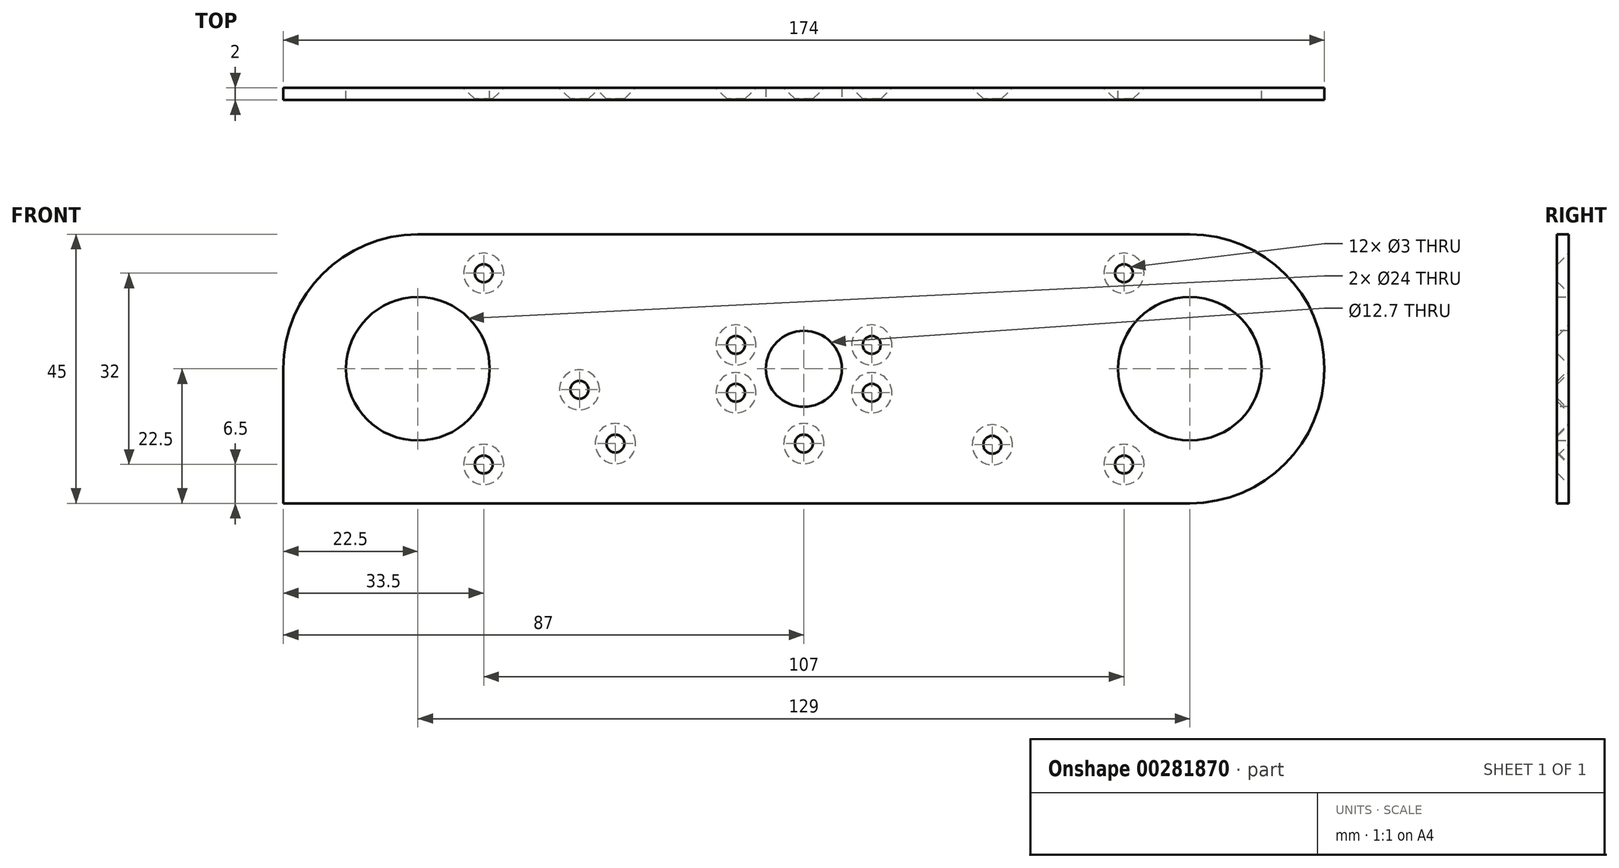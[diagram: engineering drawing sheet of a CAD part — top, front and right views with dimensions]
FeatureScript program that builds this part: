
annotation { "Feature Type Name" : "Feature", "Feature Type Description" : "" }
export const myFeature = defineFeature(function(context is Context, id is Id, definition is map)
    precondition{}
    {
        {
            var Q0;
            Q0=qCreatedBy(makeId("Front.planeOp"),FACE);
            var sketch = newSketch(context, id + "F0", { "sketchPlane" : qUnion([Q0])});
            skLineSegment(sketch, "E0.bottom", {"start": v(64.5, 22.5) * mm, "end": v(-64.5, 22.5) * mm});
            skLineSegment(sketch, "E0.top", {"start": v(64.5, -22.5) * mm, "end": v(-64.5, -22.5) * mm});
            skPoint(sketch, "E0.middle", {"position": v(0, 0) * mm});
            skCircle(sketch, "E1", {"center": v(64.5, 0) * mm, "radius": 12 * mm});
            skCircle(sketch, "E2", {"center": v(-64.5, 0) * mm, "radius": 12 * mm});
            skArc(sketch, "E3", {"start": v(-64.5, 22.5) * mm, "mid": v(-87, 0) * mm, "end": v(-64.5, -22.5) * mm});
            skArc(sketch, "E4", {"start": v(64.5, -22.5) * mm, "mid": v(87, 0) * mm, "end": v(64.5, 22.5) * mm});
            skPoint(sketch, "E5.orphan", {"position": v(-81.5, 22.5) * mm});
            skPoint(sketch, "E6.orphan", {"position": v(-81.5, -22.5) * mm});
            skPoint(sketch, "E7.orphan", {"position": v(81.5, 22.5) * mm});
            skPoint(sketch, "E8.orphan", {"position": v(81.5, -22.5) * mm});
            skSolve(sketch);
        }
        {
            var Q0;
            Q0=qSketchRegion(id+"F0",true);
            extrude(context, id + "F1", {"entities" : qUnion([Q0]), "depth" : 2 * mm});
        }
        {
            var Q0;
            Q0=makeQuery(id+"F1.opExtrude","CAP_FACE",FACE,{"disambiguationData":[OSD([sQuery(id+"F0.wireOp",EDGE,"E0.bottom"),sQuery(id+"F0.wireOp",EDGE,"E0.top"),sQuery(id+"F0.wireOp",EDGE,"E1"),sQuery(id+"F0.wireOp",EDGE,"E2"),sQuery(id+"F0.wireOp",EDGE,"E3"),sQuery(id+"F0.wireOp",EDGE,"E4")])],"isStart":false});
            var sketch = newSketch(context, id + "F2", { "sketchPlane" : qUnion([Q0])});
            skLineSegment(sketch, "E9.top", {"start": v(-64.5, -22.5) * mm, "end": v(-87, -22.5) * mm});
            skLineSegment(sketch, "E9.right", {"start": v(-87, 0) * mm, "end": v(-87, -22.5) * mm});
            skPoint(sketch, "E9.left.start.orphan", {"position": v(-64.5, 0) * mm});
            skLineSegment(sketch, "E10", {"start": v(-87, 0) * mm, "end": v(-80.88, 0) * mm});
            skLineSegment(sketch, "E11", {"start": v(-80.88, 0) * mm, "end": v(-78.27, -9.46) * mm});
            skLineSegment(sketch, "E12", {"start": v(-78.27, -9.46) * mm, "end": v(-70.55, -14.76) * mm});
            skLineSegment(sketch, "E13", {"start": v(-70.55, -14.76) * mm, "end": v(-64.5, -17.43) * mm});
            skLineSegment(sketch, "E14", {"start": v(-64.5, -17.43) * mm, "end": v(-64.5, -22.5) * mm});
            skSolve(sketch);
        }
        {
            var Q0;
            Q0=qSketchRegion(id+"F2",true);
            extrude(context, id + "F3", {"entities" : qUnion([Q0]), "operationType" : NewBodyOperationType.ADD, "oppositeDirection" : true, "depth" : 2 * mm});
        }
        {
            var Q0;
            Q0=makeQuery(id+"F3.boolean.opBoolean","MERGE",FACE,{"derivedFrom":[makeQuery(id+"F1.opExtrude","CAP_FACE",FACE,{"disambiguationData":[OSD([sQuery(id+"F0.wireOp",EDGE,"E0.bottom"),sQuery(id+"F0.wireOp",EDGE,"E0.top"),sQuery(id+"F0.wireOp",EDGE,"E1"),sQuery(id+"F0.wireOp",EDGE,"E2"),sQuery(id+"F0.wireOp",EDGE,"E3"),sQuery(id+"F0.wireOp",EDGE,"E4")])],"isStart":false}),makeQuery(id+"F3.opExtrude","CAP_FACE",FACE,{"disambiguationData":[OSD([sQuery(id+"F2.wireOp",EDGE,"E9.top"),sQuery(id+"F2.wireOp",EDGE,"E9.right"),sQuery(id+"F2.wireOp",EDGE,"E10"),sQuery(id+"F2.wireOp",EDGE,"E11"),sQuery(id+"F2.wireOp",EDGE,"E12"),sQuery(id+"F2.wireOp",EDGE,"E13"),sQuery(id+"F2.wireOp",EDGE,"E14")])],"isStart":true})]});
            var sketch = newSketch(context, id + "F4", { "sketchPlane" : qUnion([Q0])});
            skLineSegment(sketch, "E15.bottom", {"start": v(47, 22.5) * mm, "end": v(-47, 22.5) * mm, "construction": true});
            skLineSegment(sketch, "E15.top", {"start": v(47, -22.5) * mm, "end": v(-47, -22.5) * mm, "construction": true});
            skLineSegment(sketch, "E15.left", {"start": v(47, 22.5) * mm, "end": v(47, -22.5) * mm, "construction": true});
            skLineSegment(sketch, "E15.right", {"start": v(-47, 22.5) * mm, "end": v(-47, -22.5) * mm, "construction": true});
            skPoint(sketch, "E15.middle", {"position": v(0, 0) * mm});
            skLineSegment(sketch, "E16", {"start": v(-52.5, 0) * mm, "end": v(52.5, 0) * mm, "construction": true});
            skCircle(sketch, "E17", {"center": v(-53.5, 16) * mm, "radius": 1.5 * mm});
            skCircle(sketch, "E18", {"center": v(-53.5, -16) * mm, "radius": 1.5 * mm});
            skCircle(sketch, "E19", {"center": v(53.5, 16) * mm, "radius": 1.5 * mm});
            skCircle(sketch, "E20", {"center": v(53.5, -16) * mm, "radius": 1.5 * mm});
            skSolve(sketch);
        }
        {
            var Q0;
            Q0=qSketchRegion(id+"F4",true);
            extrude(context, id + "F5", {"entities" : qUnion([Q0]), "operationType" : NewBodyOperationType.REMOVE, "oppositeDirection" : true, "depth" : 25 * mm});
        }
        {
            var Q0;
            Q0=makeQuery(id+"F3.boolean.opBoolean","MERGE",FACE,{"derivedFrom":[makeQuery(id+"F1.opExtrude","CAP_FACE",FACE,{"disambiguationData":[OSD([sQuery(id+"F0.wireOp",EDGE,"E0.bottom"),sQuery(id+"F0.wireOp",EDGE,"E0.top"),sQuery(id+"F0.wireOp",EDGE,"E1"),sQuery(id+"F0.wireOp",EDGE,"E2"),sQuery(id+"F0.wireOp",EDGE,"E3"),sQuery(id+"F0.wireOp",EDGE,"E4")])],"isStart":false}),makeQuery(id+"F3.opExtrude","CAP_FACE",FACE,{"disambiguationData":[OSD([sQuery(id+"F2.wireOp",EDGE,"E9.top"),sQuery(id+"F2.wireOp",EDGE,"E9.right"),sQuery(id+"F2.wireOp",EDGE,"E10"),sQuery(id+"F2.wireOp",EDGE,"E11"),sQuery(id+"F2.wireOp",EDGE,"E12"),sQuery(id+"F2.wireOp",EDGE,"E13"),sQuery(id+"F2.wireOp",EDGE,"E14")])],"isStart":true})]});
            var sketch = newSketch(context, id + "F6", { "sketchPlane" : qUnion([Q0])});
            skCircle(sketch, "E21", {"center": v(0, 0) * mm, "radius": 6.35 * mm});
            skSolve(sketch);
        }
        {
            var Q0;
            Q0=qSketchRegion(id+"F6",true);
            extrude(context, id + "F7", {"entities" : qUnion([Q0]), "operationType" : NewBodyOperationType.REMOVE, "oppositeDirection" : true, "depth" : 25 * mm});
        }
        {
            var Q0;
            Q0=makeQuery(id+"F3.boolean.opBoolean","MERGE",FACE,{"derivedFrom":[makeQuery(id+"F1.opExtrude","CAP_FACE",FACE,{"disambiguationData":[OSD([sQuery(id+"F0.wireOp",EDGE,"E0.bottom"),sQuery(id+"F0.wireOp",EDGE,"E0.top"),sQuery(id+"F0.wireOp",EDGE,"E1"),sQuery(id+"F0.wireOp",EDGE,"E2"),sQuery(id+"F0.wireOp",EDGE,"E3"),sQuery(id+"F0.wireOp",EDGE,"E4")])],"isStart":false}),makeQuery(id+"F3.opExtrude","CAP_FACE",FACE,{"disambiguationData":[OSD([sQuery(id+"F2.wireOp",EDGE,"E9.top"),sQuery(id+"F2.wireOp",EDGE,"E9.right"),sQuery(id+"F2.wireOp",EDGE,"E10"),sQuery(id+"F2.wireOp",EDGE,"E11"),sQuery(id+"F2.wireOp",EDGE,"E12"),sQuery(id+"F2.wireOp",EDGE,"E13"),sQuery(id+"F2.wireOp",EDGE,"E14")])],"isStart":true})]});
            var sketch = newSketch(context, id + "F8", { "sketchPlane" : qUnion([Q0])});
            skPoint(sketch, "E22.middle", {"position": v(0, 0) * mm});
            skCircle(sketch, "E23", {"center": v(-11.35, 4) * mm, "radius": 1.5 * mm});
            skCircle(sketch, "E24", {"center": v(-11.35, -4) * mm, "radius": 1.5 * mm});
            skCircle(sketch, "E25", {"center": v(11.35, 4) * mm, "radius": 1.5 * mm});
            skCircle(sketch, "E26", {"center": v(11.35, -4) * mm, "radius": 1.5 * mm});
            skPoint(sketch, "E27.orphan", {"position": v(-11.35, 11.35) * mm});
            skPoint(sketch, "E28.orphan", {"position": v(11.35, 11.35) * mm});
            skPoint(sketch, "E22.top.start.orphan", {"position": v(11.35, -11.35) * mm});
            skPoint(sketch, "E29.orphan", {"position": v(-11.35, -11.35) * mm});
            skLineSegment(sketch, "E30", {"start": v(52.5, 0) * mm, "end": v(-52.5, 0) * mm, "construction": true});
            skLineSegment(sketch, "E31", {"start": v(-52.5, 0) * mm, "end": v(0, 0) * mm, "construction": true});
            skLineSegment(sketch, "E32", {"start": v(0, 22.5) * mm, "end": v(0, -22.5) * mm, "construction": true});
            skLineSegment(sketch, "E33.bottom", {"start": v(11.35, 11.35) * mm, "end": v(-11.35, 11.35) * mm, "construction": true});
            skLineSegment(sketch, "E33.top", {"start": v(11.35, -11.35) * mm, "end": v(-11.35, -11.35) * mm, "construction": true});
            skLineSegment(sketch, "E33.left", {"start": v(11.35, 11.35) * mm, "end": v(11.35, -11.35) * mm, "construction": true});
            skLineSegment(sketch, "E33.right", {"start": v(-11.35, 11.35) * mm, "end": v(-11.35, -11.35) * mm, "construction": true});
            skSolve(sketch);
        }
        {
            var Q0;
            Q0=qSketchRegion(id+"F8",true);
            extrude(context, id + "F9", {"entities" : qUnion([Q0]), "operationType" : NewBodyOperationType.REMOVE, "oppositeDirection" : true, "depth" : 25 * mm});
        }
        {
            var Q0;
            Q0=makeQuery(id+"F3.boolean.opBoolean","MERGE",FACE,{"derivedFrom":[makeQuery(id+"F1.opExtrude","CAP_FACE",FACE,{"disambiguationData":[OSD([sQuery(id+"F0.wireOp",EDGE,"E0.bottom"),sQuery(id+"F0.wireOp",EDGE,"E0.top"),sQuery(id+"F0.wireOp",EDGE,"E1"),sQuery(id+"F0.wireOp",EDGE,"E2"),sQuery(id+"F0.wireOp",EDGE,"E3"),sQuery(id+"F0.wireOp",EDGE,"E4")])],"isStart":false}),makeQuery(id+"F3.opExtrude","CAP_FACE",FACE,{"disambiguationData":[OSD([sQuery(id+"F2.wireOp",EDGE,"E9.top"),sQuery(id+"F2.wireOp",EDGE,"E9.right"),sQuery(id+"F2.wireOp",EDGE,"E10"),sQuery(id+"F2.wireOp",EDGE,"E11"),sQuery(id+"F2.wireOp",EDGE,"E12"),sQuery(id+"F2.wireOp",EDGE,"E13"),sQuery(id+"F2.wireOp",EDGE,"E14")])],"isStart":true})]});
            var sketch = newSketch(context, id + "F10", { "sketchPlane" : qUnion([Q0])});
            skCircle(sketch, "E34", {"center": v(0, -12.5) * mm, "radius": 1.5 * mm});
            skCircle(sketch, "E35", {"center": v(31.5, -12.7) * mm, "radius": 1.5 * mm});
            skCircle(sketch, "E36", {"center": v(-31.5, -12.5) * mm, "radius": 1.5 * mm});
            skLineSegment(sketch, "E37", {"start": v(-31.5, -12.5) * mm, "end": v(-43.5, -12.5) * mm, "construction": true});
            skLineSegment(sketch, "E38", {"start": v(-37.5, -12.5) * mm, "end": v(-37.5, -3.5) * mm, "construction": true});
            skCircle(sketch, "E39", {"center": v(-37.5, -3.5) * mm, "radius": 1.5 * mm});
            skSolve(sketch);
        }
        {
            var Q0;
            Q0=qSketchRegion(id+"F10",true);
            extrude(context, id + "F11", {"entities" : qUnion([Q0]), "operationType" : NewBodyOperationType.REMOVE, "oppositeDirection" : true, "depth" : 25 * mm});
        }
        {
            var Q0;
            Q0=makeQuery(id+"F5.boolean.opBoolean","INTERSECT",EDGE,{"derivedFrom":[makeQuery(id+"F3.boolean.opBoolean","MERGE",FACE,{"derivedFrom":[makeQuery(id+"F1.opExtrude","CAP_FACE",FACE,{"disambiguationData":[OSD([sQuery(id+"F0.wireOp",EDGE,"E0.bottom"),sQuery(id+"F0.wireOp",EDGE,"E0.top"),sQuery(id+"F0.wireOp",EDGE,"E1"),sQuery(id+"F0.wireOp",EDGE,"E2"),sQuery(id+"F0.wireOp",EDGE,"E3"),sQuery(id+"F0.wireOp",EDGE,"E4")])],"isStart":true}),makeQuery(id+"F3.opExtrude","CAP_FACE",FACE,{"disambiguationData":[OSD([sQuery(id+"F2.wireOp",EDGE,"E9.top"),sQuery(id+"F2.wireOp",EDGE,"E9.right"),sQuery(id+"F2.wireOp",EDGE,"E10"),sQuery(id+"F2.wireOp",EDGE,"E11"),sQuery(id+"F2.wireOp",EDGE,"E12"),sQuery(id+"F2.wireOp",EDGE,"E13"),sQuery(id+"F2.wireOp",EDGE,"E14")])],"isStart":false})]}),makeQuery(id+"F5.opExtrude","SWEPT_FACE",FACE,{"disambiguationData":[OSD([sQuery(id+"F4.wireOp",EDGE,"E18")])]})]});
            var Q1;
            Q1=makeQuery(id+"F11.boolean.opBoolean","INTERSECT",EDGE,{"derivedFrom":[makeQuery(id+"F3.boolean.opBoolean","MERGE",FACE,{"derivedFrom":[makeQuery(id+"F1.opExtrude","CAP_FACE",FACE,{"disambiguationData":[OSD([sQuery(id+"F0.wireOp",EDGE,"E0.bottom"),sQuery(id+"F0.wireOp",EDGE,"E0.top"),sQuery(id+"F0.wireOp",EDGE,"E1"),sQuery(id+"F0.wireOp",EDGE,"E2"),sQuery(id+"F0.wireOp",EDGE,"E3"),sQuery(id+"F0.wireOp",EDGE,"E4")])],"isStart":true}),makeQuery(id+"F3.opExtrude","CAP_FACE",FACE,{"disambiguationData":[OSD([sQuery(id+"F2.wireOp",EDGE,"E9.top"),sQuery(id+"F2.wireOp",EDGE,"E9.right"),sQuery(id+"F2.wireOp",EDGE,"E10"),sQuery(id+"F2.wireOp",EDGE,"E11"),sQuery(id+"F2.wireOp",EDGE,"E12"),sQuery(id+"F2.wireOp",EDGE,"E13"),sQuery(id+"F2.wireOp",EDGE,"E14")])],"isStart":false})]}),makeQuery(id+"F11.opExtrude","SWEPT_FACE",FACE,{"disambiguationData":[OSD([sQuery(id+"F10.wireOp",EDGE,"E36")])]})]});
            var Q2;
            Q2=makeQuery(id+"F5.boolean.opBoolean","INTERSECT",EDGE,{"derivedFrom":[makeQuery(id+"F3.boolean.opBoolean","MERGE",FACE,{"derivedFrom":[makeQuery(id+"F1.opExtrude","CAP_FACE",FACE,{"disambiguationData":[OSD([sQuery(id+"F0.wireOp",EDGE,"E0.bottom"),sQuery(id+"F0.wireOp",EDGE,"E0.top"),sQuery(id+"F0.wireOp",EDGE,"E1"),sQuery(id+"F0.wireOp",EDGE,"E2"),sQuery(id+"F0.wireOp",EDGE,"E3"),sQuery(id+"F0.wireOp",EDGE,"E4")])],"isStart":true}),makeQuery(id+"F3.opExtrude","CAP_FACE",FACE,{"disambiguationData":[OSD([sQuery(id+"F2.wireOp",EDGE,"E9.top"),sQuery(id+"F2.wireOp",EDGE,"E9.right"),sQuery(id+"F2.wireOp",EDGE,"E10"),sQuery(id+"F2.wireOp",EDGE,"E11"),sQuery(id+"F2.wireOp",EDGE,"E12"),sQuery(id+"F2.wireOp",EDGE,"E13"),sQuery(id+"F2.wireOp",EDGE,"E14")])],"isStart":false})]}),makeQuery(id+"F5.opExtrude","SWEPT_FACE",FACE,{"disambiguationData":[OSD([sQuery(id+"F4.wireOp",EDGE,"E17")])]})]});
            var Q3;
            Q3=makeQuery(id+"F9.boolean.opBoolean","INTERSECT",EDGE,{"derivedFrom":[makeQuery(id+"F3.boolean.opBoolean","MERGE",FACE,{"derivedFrom":[makeQuery(id+"F1.opExtrude","CAP_FACE",FACE,{"disambiguationData":[OSD([sQuery(id+"F0.wireOp",EDGE,"E0.bottom"),sQuery(id+"F0.wireOp",EDGE,"E0.top"),sQuery(id+"F0.wireOp",EDGE,"E1"),sQuery(id+"F0.wireOp",EDGE,"E2"),sQuery(id+"F0.wireOp",EDGE,"E3"),sQuery(id+"F0.wireOp",EDGE,"E4")])],"isStart":true}),makeQuery(id+"F3.opExtrude","CAP_FACE",FACE,{"disambiguationData":[OSD([sQuery(id+"F2.wireOp",EDGE,"E9.top"),sQuery(id+"F2.wireOp",EDGE,"E9.right"),sQuery(id+"F2.wireOp",EDGE,"E10"),sQuery(id+"F2.wireOp",EDGE,"E11"),sQuery(id+"F2.wireOp",EDGE,"E12"),sQuery(id+"F2.wireOp",EDGE,"E13"),sQuery(id+"F2.wireOp",EDGE,"E14")])],"isStart":false})]}),makeQuery(id+"F9.opExtrude","SWEPT_FACE",FACE,{"disambiguationData":[OSD([sQuery(id+"F8.wireOp",EDGE,"E24")])]})]});
            var Q4;
            Q4=makeQuery(id+"F9.boolean.opBoolean","INTERSECT",EDGE,{"derivedFrom":[makeQuery(id+"F3.boolean.opBoolean","MERGE",FACE,{"derivedFrom":[makeQuery(id+"F1.opExtrude","CAP_FACE",FACE,{"disambiguationData":[OSD([sQuery(id+"F0.wireOp",EDGE,"E0.bottom"),sQuery(id+"F0.wireOp",EDGE,"E0.top"),sQuery(id+"F0.wireOp",EDGE,"E1"),sQuery(id+"F0.wireOp",EDGE,"E2"),sQuery(id+"F0.wireOp",EDGE,"E3"),sQuery(id+"F0.wireOp",EDGE,"E4")])],"isStart":true}),makeQuery(id+"F3.opExtrude","CAP_FACE",FACE,{"disambiguationData":[OSD([sQuery(id+"F2.wireOp",EDGE,"E9.top"),sQuery(id+"F2.wireOp",EDGE,"E9.right"),sQuery(id+"F2.wireOp",EDGE,"E10"),sQuery(id+"F2.wireOp",EDGE,"E11"),sQuery(id+"F2.wireOp",EDGE,"E12"),sQuery(id+"F2.wireOp",EDGE,"E13"),sQuery(id+"F2.wireOp",EDGE,"E14")])],"isStart":false})]}),makeQuery(id+"F9.opExtrude","SWEPT_FACE",FACE,{"disambiguationData":[OSD([sQuery(id+"F8.wireOp",EDGE,"E23")])]})]});
            var Q5;
            Q5=makeQuery(id+"F11.boolean.opBoolean","INTERSECT",EDGE,{"derivedFrom":[makeQuery(id+"F3.boolean.opBoolean","MERGE",FACE,{"derivedFrom":[makeQuery(id+"F1.opExtrude","CAP_FACE",FACE,{"disambiguationData":[OSD([sQuery(id+"F0.wireOp",EDGE,"E0.bottom"),sQuery(id+"F0.wireOp",EDGE,"E0.top"),sQuery(id+"F0.wireOp",EDGE,"E1"),sQuery(id+"F0.wireOp",EDGE,"E2"),sQuery(id+"F0.wireOp",EDGE,"E3"),sQuery(id+"F0.wireOp",EDGE,"E4")])],"isStart":true}),makeQuery(id+"F3.opExtrude","CAP_FACE",FACE,{"disambiguationData":[OSD([sQuery(id+"F2.wireOp",EDGE,"E9.top"),sQuery(id+"F2.wireOp",EDGE,"E9.right"),sQuery(id+"F2.wireOp",EDGE,"E10"),sQuery(id+"F2.wireOp",EDGE,"E11"),sQuery(id+"F2.wireOp",EDGE,"E12"),sQuery(id+"F2.wireOp",EDGE,"E13"),sQuery(id+"F2.wireOp",EDGE,"E14")])],"isStart":false})]}),makeQuery(id+"F11.opExtrude","SWEPT_FACE",FACE,{"disambiguationData":[OSD([sQuery(id+"F10.wireOp",EDGE,"E34")])]})]});
            var Q6;
            Q6=makeQuery(id+"F9.boolean.opBoolean","INTERSECT",EDGE,{"derivedFrom":[makeQuery(id+"F3.boolean.opBoolean","MERGE",FACE,{"derivedFrom":[makeQuery(id+"F1.opExtrude","CAP_FACE",FACE,{"disambiguationData":[OSD([sQuery(id+"F0.wireOp",EDGE,"E0.bottom"),sQuery(id+"F0.wireOp",EDGE,"E0.top"),sQuery(id+"F0.wireOp",EDGE,"E1"),sQuery(id+"F0.wireOp",EDGE,"E2"),sQuery(id+"F0.wireOp",EDGE,"E3"),sQuery(id+"F0.wireOp",EDGE,"E4")])],"isStart":true}),makeQuery(id+"F3.opExtrude","CAP_FACE",FACE,{"disambiguationData":[OSD([sQuery(id+"F2.wireOp",EDGE,"E9.top"),sQuery(id+"F2.wireOp",EDGE,"E9.right"),sQuery(id+"F2.wireOp",EDGE,"E10"),sQuery(id+"F2.wireOp",EDGE,"E11"),sQuery(id+"F2.wireOp",EDGE,"E12"),sQuery(id+"F2.wireOp",EDGE,"E13"),sQuery(id+"F2.wireOp",EDGE,"E14")])],"isStart":false})]}),makeQuery(id+"F9.opExtrude","SWEPT_FACE",FACE,{"disambiguationData":[OSD([sQuery(id+"F8.wireOp",EDGE,"E26")])]})]});
            var Q7;
            Q7=makeQuery(id+"F9.boolean.opBoolean","INTERSECT",EDGE,{"derivedFrom":[makeQuery(id+"F3.boolean.opBoolean","MERGE",FACE,{"derivedFrom":[makeQuery(id+"F1.opExtrude","CAP_FACE",FACE,{"disambiguationData":[OSD([sQuery(id+"F0.wireOp",EDGE,"E0.bottom"),sQuery(id+"F0.wireOp",EDGE,"E0.top"),sQuery(id+"F0.wireOp",EDGE,"E1"),sQuery(id+"F0.wireOp",EDGE,"E2"),sQuery(id+"F0.wireOp",EDGE,"E3"),sQuery(id+"F0.wireOp",EDGE,"E4")])],"isStart":true}),makeQuery(id+"F3.opExtrude","CAP_FACE",FACE,{"disambiguationData":[OSD([sQuery(id+"F2.wireOp",EDGE,"E9.top"),sQuery(id+"F2.wireOp",EDGE,"E9.right"),sQuery(id+"F2.wireOp",EDGE,"E10"),sQuery(id+"F2.wireOp",EDGE,"E11"),sQuery(id+"F2.wireOp",EDGE,"E12"),sQuery(id+"F2.wireOp",EDGE,"E13"),sQuery(id+"F2.wireOp",EDGE,"E14")])],"isStart":false})]}),makeQuery(id+"F9.opExtrude","SWEPT_FACE",FACE,{"disambiguationData":[OSD([sQuery(id+"F8.wireOp",EDGE,"E25")])]})]});
            var Q8;
            Q8=makeQuery(id+"F11.boolean.opBoolean","INTERSECT",EDGE,{"derivedFrom":[makeQuery(id+"F3.boolean.opBoolean","MERGE",FACE,{"derivedFrom":[makeQuery(id+"F1.opExtrude","CAP_FACE",FACE,{"disambiguationData":[OSD([sQuery(id+"F0.wireOp",EDGE,"E0.bottom"),sQuery(id+"F0.wireOp",EDGE,"E0.top"),sQuery(id+"F0.wireOp",EDGE,"E1"),sQuery(id+"F0.wireOp",EDGE,"E2"),sQuery(id+"F0.wireOp",EDGE,"E3"),sQuery(id+"F0.wireOp",EDGE,"E4")])],"isStart":true}),makeQuery(id+"F3.opExtrude","CAP_FACE",FACE,{"disambiguationData":[OSD([sQuery(id+"F2.wireOp",EDGE,"E9.top"),sQuery(id+"F2.wireOp",EDGE,"E9.right"),sQuery(id+"F2.wireOp",EDGE,"E10"),sQuery(id+"F2.wireOp",EDGE,"E11"),sQuery(id+"F2.wireOp",EDGE,"E12"),sQuery(id+"F2.wireOp",EDGE,"E13"),sQuery(id+"F2.wireOp",EDGE,"E14")])],"isStart":false})]}),makeQuery(id+"F11.opExtrude","SWEPT_FACE",FACE,{"disambiguationData":[OSD([sQuery(id+"F10.wireOp",EDGE,"E35")])]})]});
            var Q9;
            Q9=makeQuery(id+"F5.boolean.opBoolean","INTERSECT",EDGE,{"derivedFrom":[makeQuery(id+"F3.boolean.opBoolean","MERGE",FACE,{"derivedFrom":[makeQuery(id+"F1.opExtrude","CAP_FACE",FACE,{"disambiguationData":[OSD([sQuery(id+"F0.wireOp",EDGE,"E0.bottom"),sQuery(id+"F0.wireOp",EDGE,"E0.top"),sQuery(id+"F0.wireOp",EDGE,"E1"),sQuery(id+"F0.wireOp",EDGE,"E2"),sQuery(id+"F0.wireOp",EDGE,"E3"),sQuery(id+"F0.wireOp",EDGE,"E4")])],"isStart":true}),makeQuery(id+"F3.opExtrude","CAP_FACE",FACE,{"disambiguationData":[OSD([sQuery(id+"F2.wireOp",EDGE,"E9.top"),sQuery(id+"F2.wireOp",EDGE,"E9.right"),sQuery(id+"F2.wireOp",EDGE,"E10"),sQuery(id+"F2.wireOp",EDGE,"E11"),sQuery(id+"F2.wireOp",EDGE,"E12"),sQuery(id+"F2.wireOp",EDGE,"E13"),sQuery(id+"F2.wireOp",EDGE,"E14")])],"isStart":false})]}),makeQuery(id+"F5.opExtrude","SWEPT_FACE",FACE,{"disambiguationData":[OSD([sQuery(id+"F4.wireOp",EDGE,"E20")])]})]});
            var Q10;
            Q10=makeQuery(id+"F5.boolean.opBoolean","INTERSECT",EDGE,{"derivedFrom":[makeQuery(id+"F3.boolean.opBoolean","MERGE",FACE,{"derivedFrom":[makeQuery(id+"F1.opExtrude","CAP_FACE",FACE,{"disambiguationData":[OSD([sQuery(id+"F0.wireOp",EDGE,"E0.bottom"),sQuery(id+"F0.wireOp",EDGE,"E0.top"),sQuery(id+"F0.wireOp",EDGE,"E1"),sQuery(id+"F0.wireOp",EDGE,"E2"),sQuery(id+"F0.wireOp",EDGE,"E3"),sQuery(id+"F0.wireOp",EDGE,"E4")])],"isStart":true}),makeQuery(id+"F3.opExtrude","CAP_FACE",FACE,{"disambiguationData":[OSD([sQuery(id+"F2.wireOp",EDGE,"E9.top"),sQuery(id+"F2.wireOp",EDGE,"E9.right"),sQuery(id+"F2.wireOp",EDGE,"E10"),sQuery(id+"F2.wireOp",EDGE,"E11"),sQuery(id+"F2.wireOp",EDGE,"E12"),sQuery(id+"F2.wireOp",EDGE,"E13"),sQuery(id+"F2.wireOp",EDGE,"E14")])],"isStart":false})]}),makeQuery(id+"F5.opExtrude","SWEPT_FACE",FACE,{"disambiguationData":[OSD([sQuery(id+"F4.wireOp",EDGE,"E19")])]})]});
            var Q11;
            Q11=makeQuery(id+"F11.boolean.opBoolean","INTERSECT",EDGE,{"derivedFrom":[makeQuery(id+"F3.boolean.opBoolean","MERGE",FACE,{"derivedFrom":[makeQuery(id+"F1.opExtrude","CAP_FACE",FACE,{"disambiguationData":[OSD([sQuery(id+"F0.wireOp",EDGE,"E0.bottom"),sQuery(id+"F0.wireOp",EDGE,"E0.top"),sQuery(id+"F0.wireOp",EDGE,"E1"),sQuery(id+"F0.wireOp",EDGE,"E2"),sQuery(id+"F0.wireOp",EDGE,"E3"),sQuery(id+"F0.wireOp",EDGE,"E4")])],"isStart":true}),makeQuery(id+"F3.opExtrude","CAP_FACE",FACE,{"disambiguationData":[OSD([sQuery(id+"F2.wireOp",EDGE,"E9.top"),sQuery(id+"F2.wireOp",EDGE,"E9.right"),sQuery(id+"F2.wireOp",EDGE,"E10"),sQuery(id+"F2.wireOp",EDGE,"E11"),sQuery(id+"F2.wireOp",EDGE,"E12"),sQuery(id+"F2.wireOp",EDGE,"E13"),sQuery(id+"F2.wireOp",EDGE,"E14")])],"isStart":false})]}),makeQuery(id+"F11.opExtrude","SWEPT_FACE",FACE,{"disambiguationData":[OSD([sQuery(id+"F10.wireOp",EDGE,"E39")])]})]});
            chamfer(context, id + "F12", {"entities" : qUnion([Q0, Q1, Q2, Q3, Q4, Q5, Q6, Q7, Q8, Q9, Q10, Q11]), "width" : 1.86 * mm, "tangentPropagation" : true});
        }
    });
